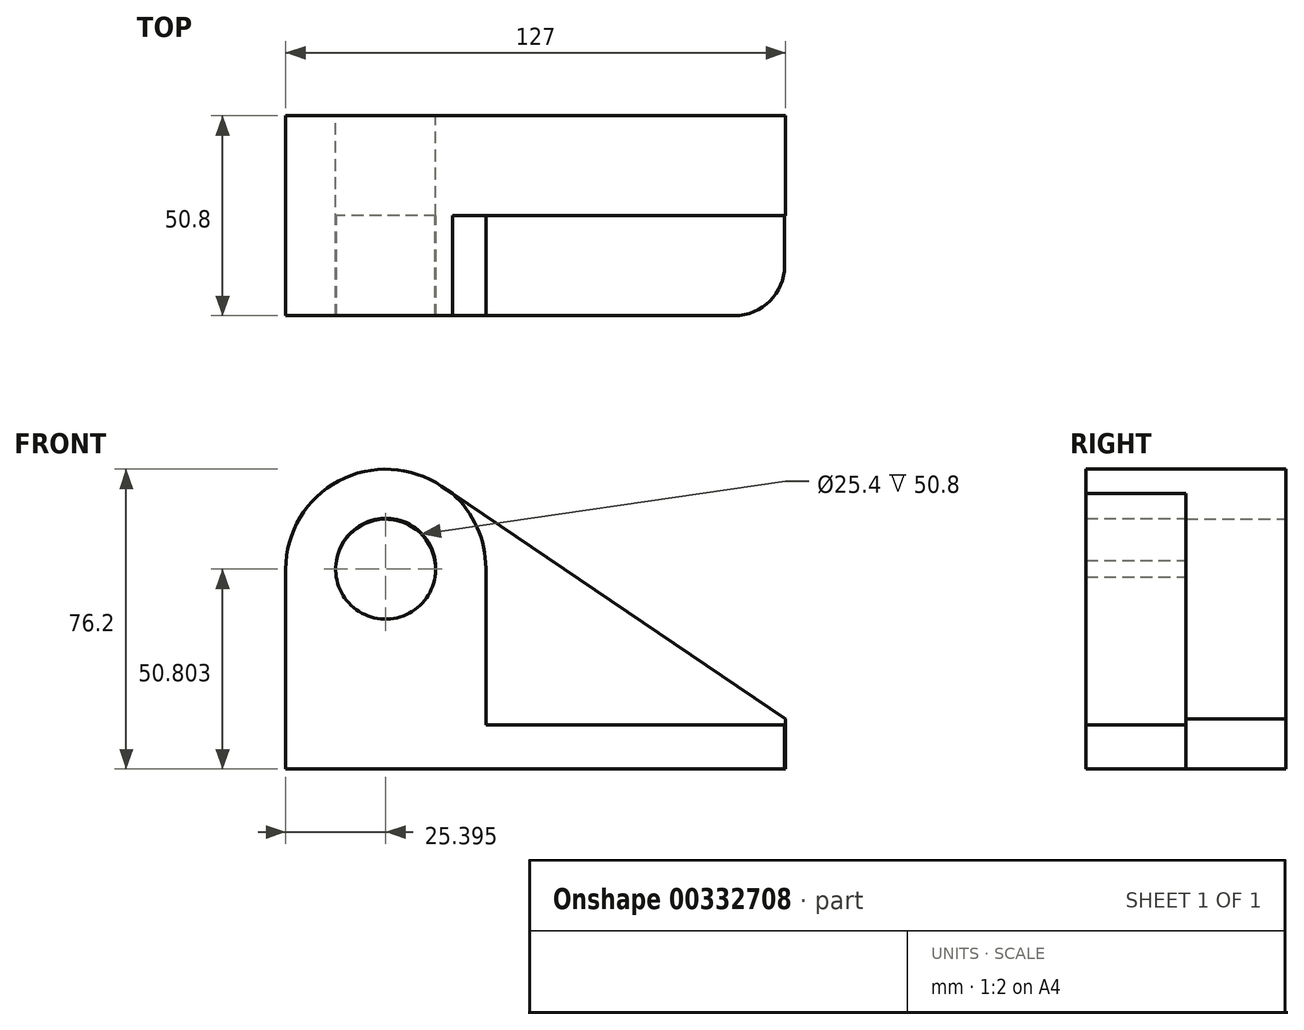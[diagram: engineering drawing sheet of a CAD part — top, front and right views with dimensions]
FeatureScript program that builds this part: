
annotation { "Feature Type Name" : "Feature", "Feature Type Description" : "" }
export const myFeature = defineFeature(function(context is Context, id is Id, definition is map)
    precondition{}
    {
        {
            var Q0;
            Q0=qCreatedBy(makeId("Front.planeOp"),FACE);
            var sketch = newSketch(context, id + "F0", { "sketchPlane" : qUnion([Q0])});
            skCircle(sketch, "E0", {"center": v(-40.6, 30.15) * mm, "radius": 12.7 * mm});
            skArc(sketch, "E1", {"start": v(-26.37, 51.19) * mm, "mid": v(-52.51, 52.59) * mm, "end": v(-66, 30.15) * mm});
            skLineSegment(sketch, "E2", {"start": v(-66, 30.15) * mm, "end": v(-66, -20.65) * mm});
            skLineSegment(sketch, "E3", {"start": v(61, -20.65) * mm, "end": v(-66, -20.65) * mm});
            skLineSegment(sketch, "E4", {"start": v(61, -7.95) * mm, "end": v(61, -20.65) * mm});
            skLineSegment(sketch, "E5", {"start": v(61, -7.95) * mm, "end": v(-26.37, 51.19) * mm});
            skSolve(sketch);
        }
        {
            var Q0;
            Q0 = qSketchRegion(id + "F0", true);
            extrude(context, id + "F1", {"entities" : qUnion([Q0]), "depth" : 25.4 * mm});
        }
        {
            var Q0;
            Q0=makeQuery(id+"F1.opExtrude","CAP_FACE",FACE,{"disambiguationData":[OSD([sQuery(id+"F0.wireOp",EDGE,"E0"),sQuery(id+"F0.wireOp",EDGE,"E1"),sQuery(id+"F0.wireOp",EDGE,"E2"),sQuery(id+"F0.wireOp",EDGE,"E3"),sQuery(id+"F0.wireOp",EDGE,"E4"),sQuery(id+"F0.wireOp",EDGE,"E5")])],"isStart":false});
            var sketch = newSketch(context, id + "F2", { "sketchPlane" : qUnion([Q0])});
            skCircle(sketch, "E6", {"center": v(-40.56, 30.4) * mm, "radius": 12.7 * mm});
            skLineSegment(sketch, "E7.bottom", {"start": v(60.75, -9.42) * mm, "end": v(-15.16, -9.42) * mm});
            skLineSegment(sketch, "E7.top", {"start": v(60.75, -20.96) * mm, "end": v(-65.9, -20.96) * mm});
            skLineSegment(sketch, "E7.left", {"start": v(60.75, -9.42) * mm, "end": v(60.75, -20.96) * mm});
            skLineSegment(sketch, "E7.right", {"start": v(-65.9, -9.42) * mm, "end": v(-65.9, -20.96) * mm});
            skLineSegment(sketch, "E8", {"start": v(-15.16, 30.4) * mm, "end": v(-15.16, -9.42) * mm});
            skArc(sketch, "E9", {"start": v(-15.16, 30.4) * mm, "mid": v(-40.56, 55.8) * mm, "end": v(-65.96, 30.4) * mm});
            skPoint(sketch, "E10.orphan", {"position": v(-65.96, 30.4) * mm});
            skSolve(sketch);
        }
        {
            var Q0;
            {var subQ16=sQuery(id+"F2.wireOp",EDGE,"E7.bottom");Q0=makeQuery(id+"F2.imprint","IMPRINT",FACE,{"disambiguationData":[TD([[makeQuery(id+"F2.imprint","IMPRINT",EDGE,{"derivedFrom":subQ16}),1.0]])]});}
            extrude(context, id + "F3", {"entities" : qUnion([Q0]), "operationType" : NewBodyOperationType.ADD, "depth" : 25.4 * mm});
        }
        {
            var Q0;
            Q0=makeQuery(id+"F3.opExtrude","CAP_EDGE",EDGE,{"disambiguationData":[OSD([sQuery(id+"F2.wireOp",EDGE,"E7.left")])],"isStart":false});
            fillet(context, id + "F4", {"entities" : qUnion([Q0]), "radius" : 12.7 * mm, "tangentPropagation" : true, "allowEdgeOverflow" : false});
        }
    });
